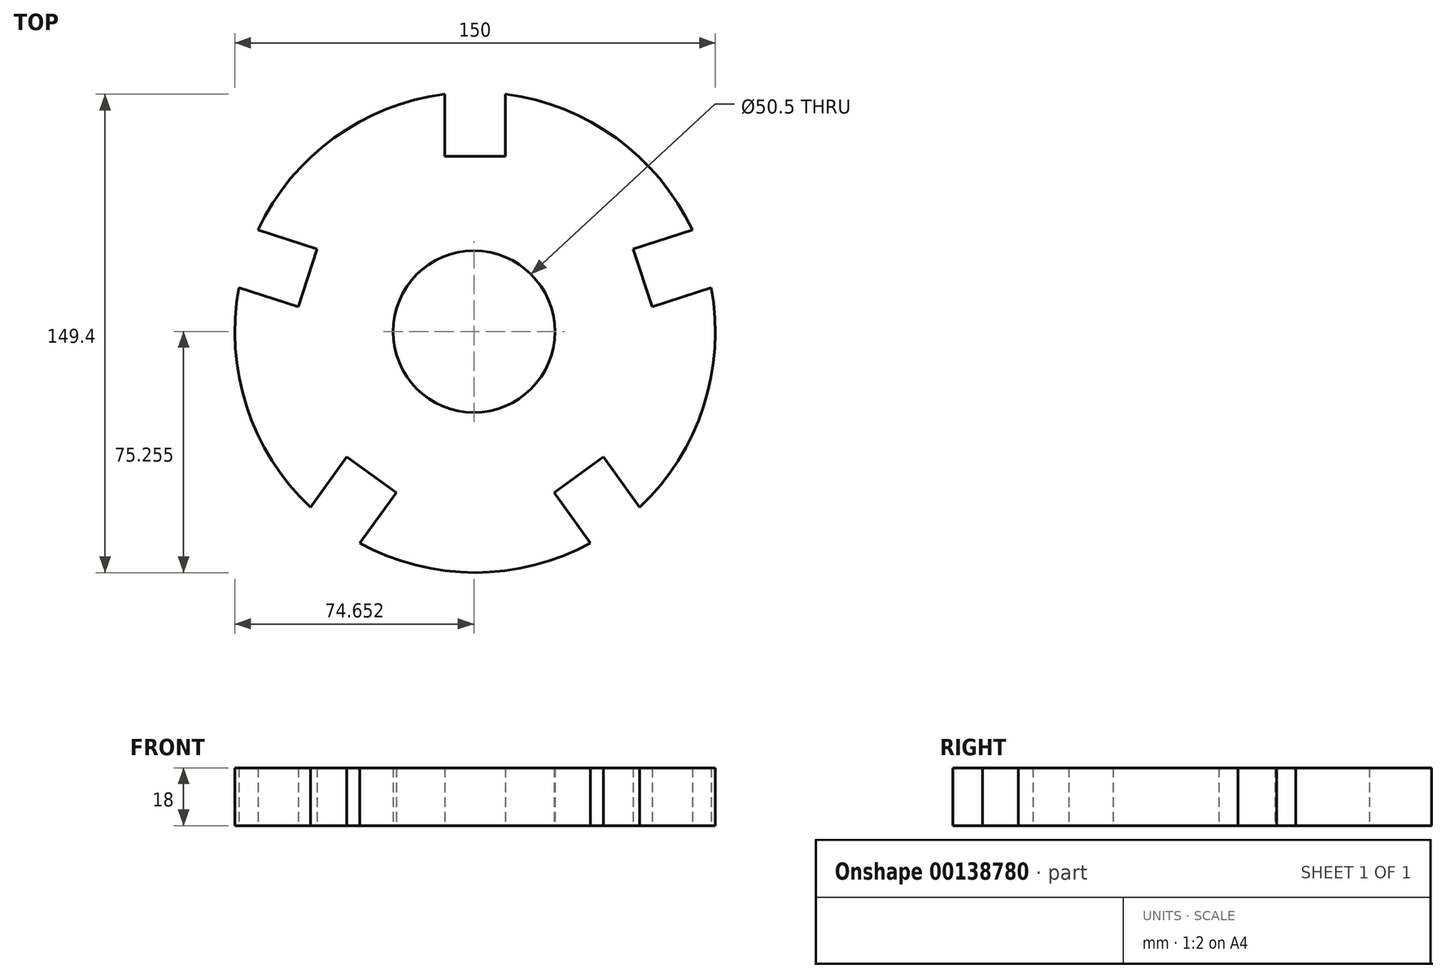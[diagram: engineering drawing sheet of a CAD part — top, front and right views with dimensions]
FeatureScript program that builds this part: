
annotation { "Feature Type Name" : "Feature", "Feature Type Description" : "" }
export const myFeature = defineFeature(function(context is Context, id is Id, definition is map)
    precondition{}
    {
        {
            var Q0;
            Q0=qCreatedBy(makeId("Top.planeOp"),FACE);
            var sketch = newSketch(context, id + "F0", { "sketchPlane" : qUnion([Q0])});
            skCircle(sketch, "E0.cCircle", {"center": v(0, 0) * mm, "radius": 25 * mm, "construction": true});
            skLineSegment(sketch, "E0.0", {"start": v(-18.16, 25) * mm, "end": v(18.16, 25) * mm, "construction": true});
            skLineSegment(sketch, "E0.1", {"start": v(18.16, 25) * mm, "end": v(29.39, -9.55) * mm, "construction": true});
            skLineSegment(sketch, "E0.2", {"start": v(29.39, -9.55) * mm, "end": v(0, -30.9) * mm, "construction": true});
            skLineSegment(sketch, "E0.3", {"start": v(0, -30.9) * mm, "end": v(-29.39, -9.55) * mm, "construction": true});
            skLineSegment(sketch, "E0.4", {"start": v(-29.39, -9.55) * mm, "end": v(-18.16, 25) * mm, "construction": true});
            skPoint(sketch, "E0.0.midPoint", {"position": v(0, 25) * mm});
            skCircle(sketch, "E1.cCircle", {"center": v(0, 0) * mm, "radius": 55 * mm, "construction": true});
            skLineSegment(sketch, "E1.0", {"start": v(-39.96, 55) * mm, "end": v(39.96, 55) * mm, "construction": true});
            skLineSegment(sketch, "E1.1", {"start": v(39.96, 55) * mm, "end": v(64.66, -21) * mm, "construction": true});
            skLineSegment(sketch, "E1.2", {"start": v(64.66, -21) * mm, "end": v(0, -67.98) * mm, "construction": true});
            skLineSegment(sketch, "E1.3", {"start": v(0, -67.98) * mm, "end": v(-64.66, -21) * mm, "construction": true});
            skLineSegment(sketch, "E1.4", {"start": v(-64.66, -21) * mm, "end": v(-39.96, 55) * mm, "construction": true});
            skPoint(sketch, "E1.0.midPoint", {"position": v(0, 55) * mm});
            skArc(sketch, "E2", {"start": v(-9.5, 74.4) * mm, "mid": v(-44.08, 60.68) * mm, "end": v(-67.82, 32.02) * mm});
            skLineSegment(sketch, "E3.bottom", {"start": v(-9.5, 55) * mm, "end": v(9.5, 55) * mm});
            skLineSegment(sketch, "E3.left", {"start": v(-9.5, 55) * mm, "end": v(-9.5, 74.4) * mm});
            skLineSegment(sketch, "E3.right", {"start": v(9.5, 55) * mm, "end": v(9.5, 74.4) * mm});
            skLineSegment(sketch, "E4.1.0", {"start": v(-49.37, 26.03) * mm, "end": v(-67.82, 32.02) * mm});
            skLineSegment(sketch, "E4.1.1", {"start": v(-55.24, 7.96) * mm, "end": v(-49.37, 26.03) * mm});
            skPoint(sketch, "E4.1.2", {"position": v(-52.3, 17) * mm});
            skLineSegment(sketch, "E4.1.3", {"start": v(-55.24, 7.96) * mm, "end": v(-73.7, 13.95) * mm});
            skLineSegment(sketch, "E4.2.0", {"start": v(-40.01, -38.91) * mm, "end": v(-51.41, -54.6) * mm});
            skLineSegment(sketch, "E4.2.1", {"start": v(-24.64, -50.08) * mm, "end": v(-40.01, -38.91) * mm});
            skPoint(sketch, "E4.2.2", {"position": v(-32.33, -44.5) * mm});
            skLineSegment(sketch, "E4.2.3", {"start": v(-24.64, -50.08) * mm, "end": v(-36.04, -65.77) * mm});
            skLineSegment(sketch, "E4.3.0", {"start": v(24.64, -50.08) * mm, "end": v(36.04, -65.77) * mm});
            skLineSegment(sketch, "E4.3.1", {"start": v(40.01, -38.91) * mm, "end": v(24.64, -50.08) * mm});
            skPoint(sketch, "E4.3.2", {"position": v(32.33, -44.5) * mm});
            skLineSegment(sketch, "E4.3.3", {"start": v(40.01, -38.91) * mm, "end": v(51.41, -54.6) * mm});
            skLineSegment(sketch, "E4.4.0", {"start": v(55.24, 7.96) * mm, "end": v(73.7, 13.95) * mm});
            skLineSegment(sketch, "E4.4.1", {"start": v(49.37, 26.03) * mm, "end": v(55.24, 7.96) * mm});
            skPoint(sketch, "E4.4.2", {"position": v(52.3, 17) * mm});
            skLineSegment(sketch, "E4.4.3", {"start": v(49.37, 26.03) * mm, "end": v(67.82, 32.02) * mm});
            skArc(sketch, "E5.trimOffspring", {"start": v(-73.7, 13.95) * mm, "mid": v(-71.33, -23.18) * mm, "end": v(-51.41, -54.6) * mm});
            skArc(sketch, "E6.trimOffspring", {"start": v(67.82, 32.02) * mm, "mid": v(44.08, 60.68) * mm, "end": v(9.5, 74.4) * mm});
            skArc(sketch, "E7.trimOffspring", {"start": v(51.41, -54.6) * mm, "mid": v(71.33, -23.18) * mm, "end": v(73.7, 13.95) * mm});
            skArc(sketch, "E8.trimOffspring", {"start": v(-36.04, -65.77) * mm, "mid": v(0, -75) * mm, "end": v(36.04, -65.77) * mm});
            skCircle(sketch, "E9", {"center": v(-0.35, 0.26) * mm, "radius": 25.25 * mm});
            skSolve(sketch);
        }
        {
            var Q0;
            Q0 = qSketchRegion(id + "F0", true);
            extrude(context, id + "F1", {"entities" : qUnion([Q0]), "depth" : 18 * mm});
        }
    });
